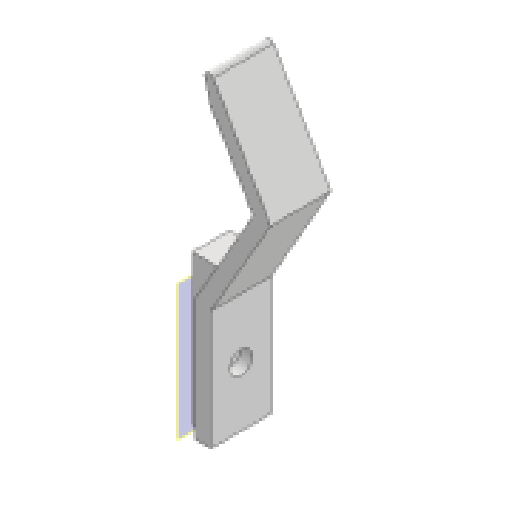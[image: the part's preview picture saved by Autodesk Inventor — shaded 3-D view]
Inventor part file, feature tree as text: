
AUTODESK INVENTOR PART (.ipt)
format: ipt  version: 2025 (Build 290162010, 162A)  size: 128,000 bytes
history: native  units: in
note: dims shown in document units (in); Inventor stores cm internally (conversion verified against a paired STEP export)
features: extrude x4, sketch x4, fillet x1, plane x1
ambient origin geometry x8: Origin, YZ Plane, XZ Plane, XY Plane, X Axis, Y Axis, Z Axis, Center Point
bodies: Solid1 (feature_tree)
feature tree (10):
  extrude  "Extrusion1"  Depth=0.2in
  fillet  "Fillet1"  Radius=0.8in
  plane  "Work Plane1"
  extrude  "Extrusion2"  Depth=0.2in
  extrude  "Extrusion3"  TaperAngle=120.0deg  [1 undecoded]
  extrude  "Extrusion4"  Depth=0.158in
  sketch  "Sketch1"  dims[d0=1.638in d1=0.2in d4=0.8in d5=0.0in]
  sketch  "Sketch2"  dims[d6=0.2in d7=0.2in]
  sketch  "Sketch3"  dims[d8=30.0deg d10=120.0deg]
  sketch  "Sketch4"  dims[d11=2.0in d12=1.525in d13=15.0deg d14=0.0625in d15=0.2in d16=0.49in d17=1.984in d18=0.245in d19=1.0in d20=0.0in d21=0.14in d22=1.0in d23=0.0in d24=0.3in d25=0.158in d26=0.0in]
note: 1 required parameter value undecoded (feature->parameter linkage not recoverable at this tier; creation-order binding heuristic only, values carry confidence <= 0.55)
